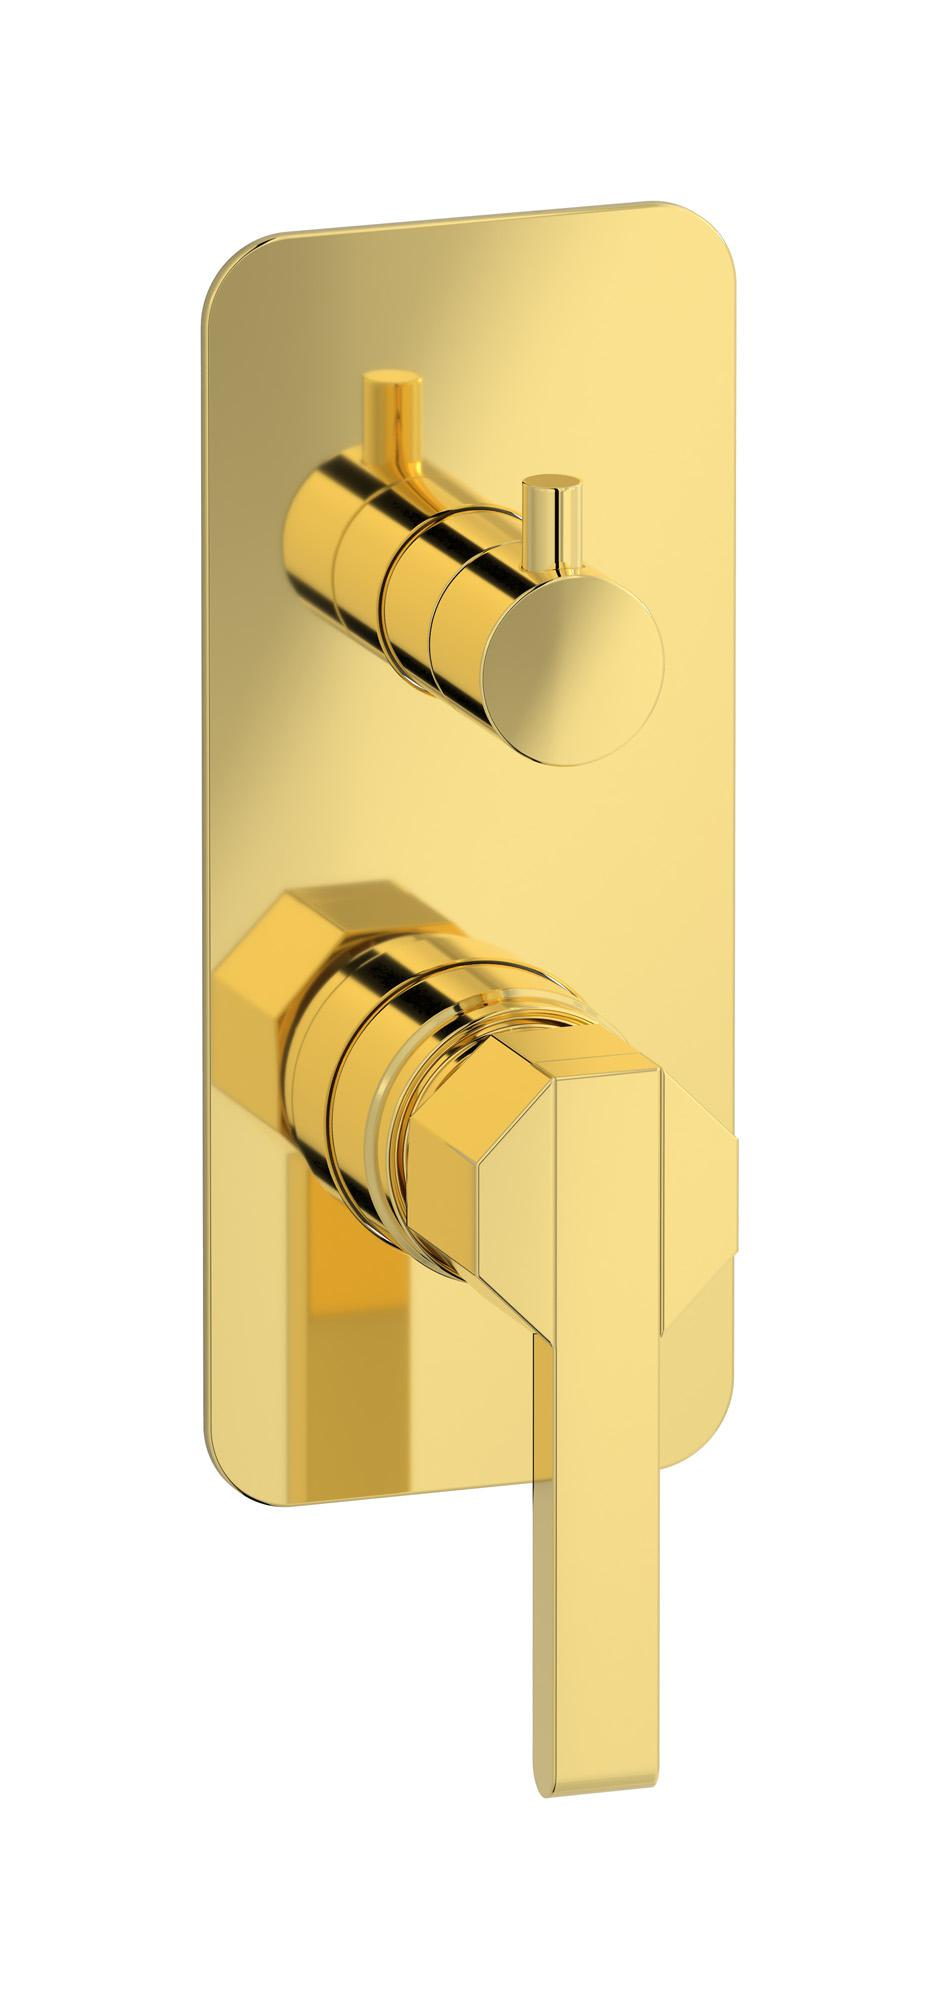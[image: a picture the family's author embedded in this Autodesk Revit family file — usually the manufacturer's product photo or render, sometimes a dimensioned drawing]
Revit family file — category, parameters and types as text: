
# Revit family: BL310
name_source: partatom
category: Apparecchi idraulici
units: mm (PartAtom-declared; Revit-internal decimal feet)

## family parameters
Basato su piano di lavoro = No
Condiviso = No
Mantieni orientamento annotazione = No
Numero OmniClass = 23.45.55.17
Punto di calcolo locali = No
Quota connettore circolare = Usa diametro
Sempre verticale = Sì
Taglio con vuoti quando caricato = No
Tipo di parte = Normale
Titolo OmniClass = Mixing Faucets

## types (7) — shared parameters
Cold water inlet = 10 mm  [stored 0.0328084 ft]
Commenti sul tipo = Wall mixer
Connessione CW = No
Connessione HW = No
Connessione di scarico = No
Connessione di ventilazione = No
Descrizione = Exposed parts for manual wall mixer with three ways diverter
Hot water inlet = 10 mm  [stored 0.0328084 ft]
Produttore = IB Rubinetterie S.p.A.
URL = https://www.weareib.it
zero-valued in all types: Prospetto di default

## per-type parameters (varying)
| type | Finishes surface | Immagine tipo | Modello |
| Chrome | IB_Chrome | BL310CC.jpg | BL310CC |
| Gold | IB_gold | BL310OO.jpg | BL310OO |
| Rose gold | IB_Rose gold | BL310RS.jpg | BL310RS |
| Platinum | IB_Platinum | BL310PL.jpg | BL310PL |
| Pale gold | IB_Pale gold | BL310II.jpg | BL310II |
| Modern Bronze | IB_Modern bronze | BL310MB.jpg | BL310MB |
| Brushed Nickel | IB_Brushed nickel | BL310SS.jpg | BL310SS |

note: [stored X ft] marks values corroborated as IEEE doubles in the binary element streams (Revit-internal decimal feet)
